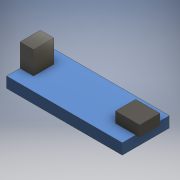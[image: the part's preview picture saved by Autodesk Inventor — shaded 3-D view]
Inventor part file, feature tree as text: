
AUTODESK INVENTOR PART (.ipt)
format: ipt  version: 2016 (Build 200138000, 138)  size: 132,608 bytes
history: native  units: mm
features: extrude x4, sketch x4
ambient origin geometry x8: Origin, YZ Plane, XZ Plane, XY Plane, X Axis, Y Axis, Z Axis, Center Point
bodies: Solid1 (feature_tree)
feature tree (8):
  extrude  "Extrusion1"  Depth=17.5mm
  extrude  "Extrusion2"  Depth=5.0mm
  extrude  "Extrusion3"  Depth=5.0mm
  extrude  "Extrusion4"  Depth=5.0mm
  sketch  "Sketch1"  dims[d0=43.0mm d1=17.5mm]
  sketch  "Sketch2"  dims[d2=4.0mm d3=0.0mm d4=5.0mm]
  sketch  "Sketch3"  dims[d5=5.0mm d6=5.0mm]
  sketch  "Sketch4"  dims[d7=8.5mm d8=0.0mm d9=5.0mm d10=7.5mm d11=5.0mm d12=4.0mm d13=0.0mm d14=1.5mm d15=0.0mm]
